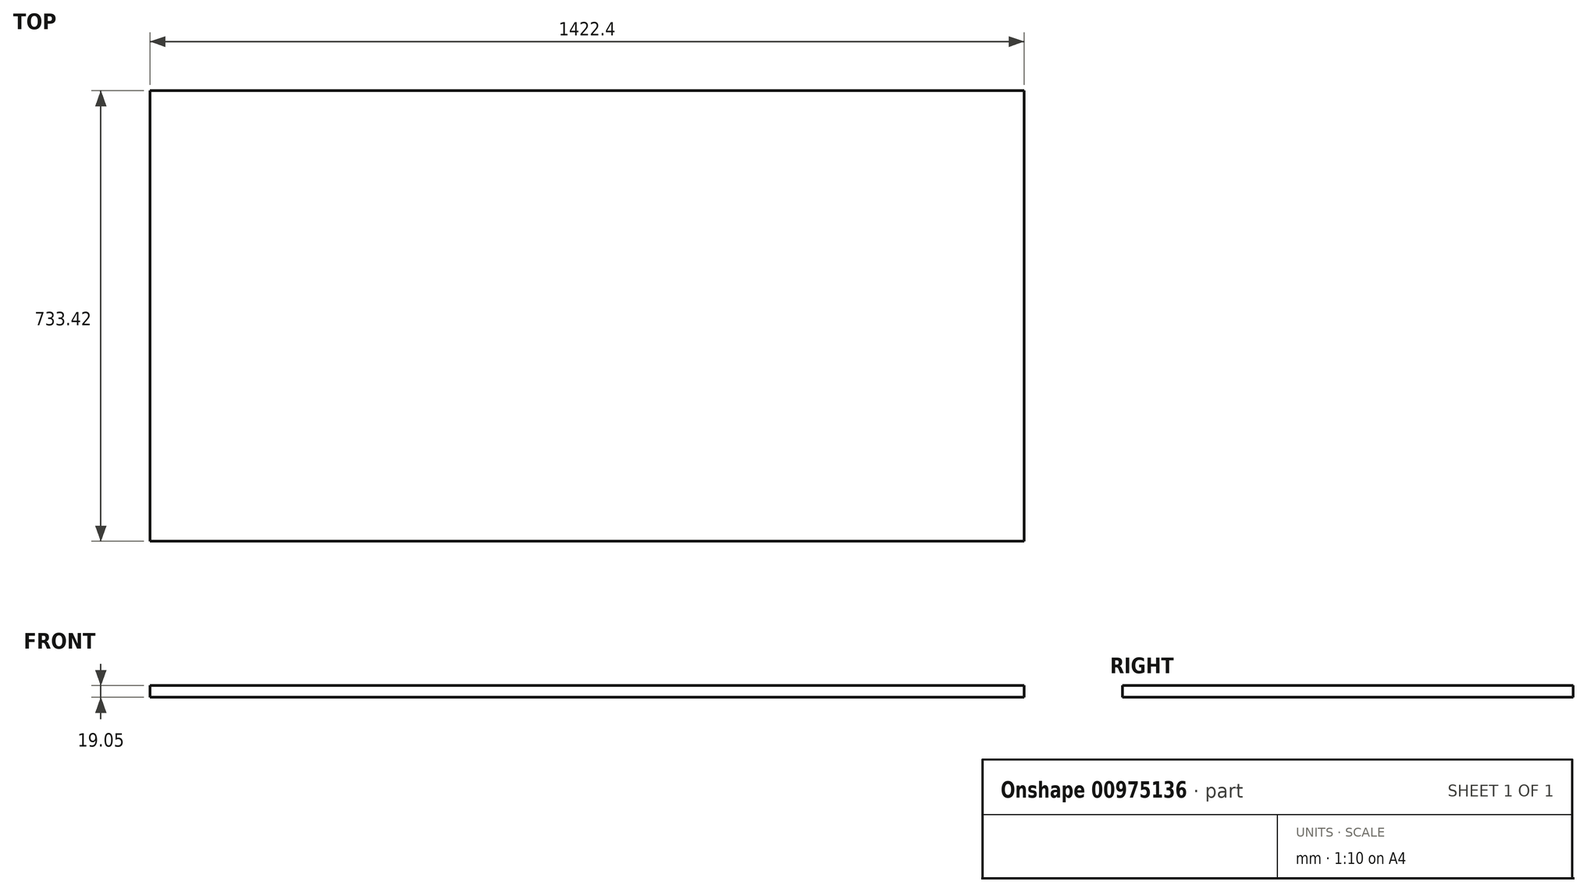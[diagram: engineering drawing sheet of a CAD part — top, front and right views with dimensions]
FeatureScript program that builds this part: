
annotation { "Feature Type Name" : "Feature", "Feature Type Description" : "" }
export const myFeature = defineFeature(function(context is Context, id is Id, definition is map)
    precondition{}
    {
        {
            var Q0;
            Q0=qCreatedBy(makeId("Top.planeOp"),FACE);
            var sketch = newSketch(context, id + "F0", { "sketchPlane" : qUnion([Q0])});
            skLineSegment(sketch, "E0.bottom", {"start": v(0, 0) * mm, "end": v(1422.4, 0) * mm});
            skLineSegment(sketch, "E0.top", {"start": v(0, 733.43) * mm, "end": v(1422.4, 733.43) * mm});
            skLineSegment(sketch, "E0.left", {"start": v(0, 0) * mm, "end": v(0, 733.43) * mm});
            skLineSegment(sketch, "E0.right", {"start": v(1422.4, 0) * mm, "end": v(1422.4, 733.43) * mm});
            skSolve(sketch);
        }
        {
            var Q0;
            Q0=makeQuery(id+"F0.imprint","IMPRINT",FACE,{"disambiguationData":[TD([[makeQuery(id+"F0.imprint","IMPRINT",EDGE,{"derivedFrom":sQuery(id+"F0.wireOp",EDGE,"E0.bottom")}),1.0]])]});
            extrude(context, id + "F1", {"entities" : qUnion([Q0]), "depth" : 19.05 * mm, "offsetDistance" : 25.4 * mm});
        }
    });
